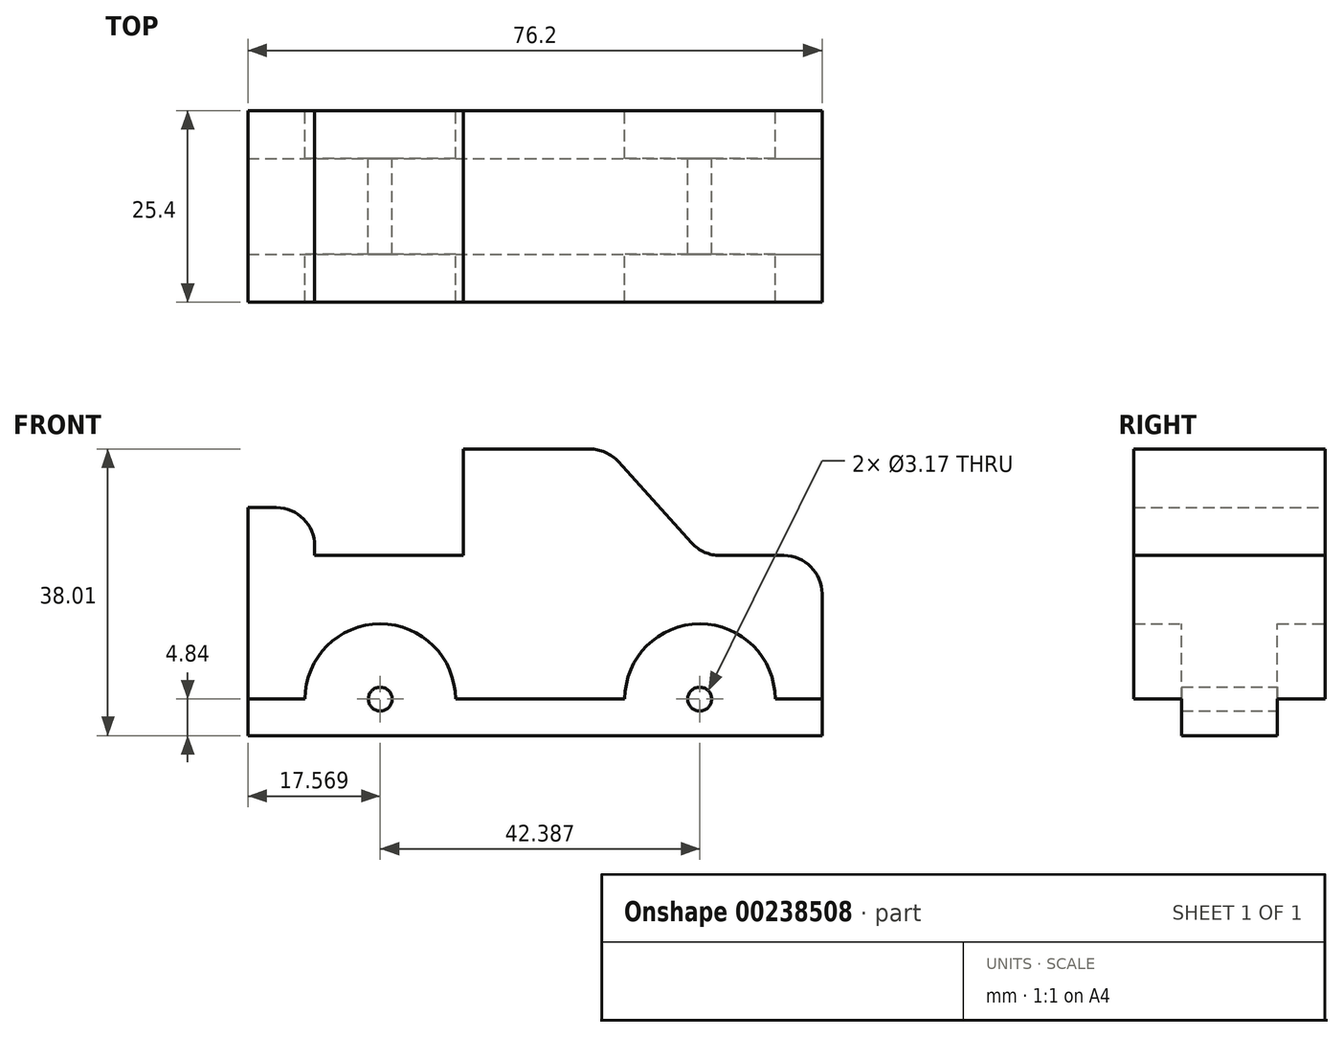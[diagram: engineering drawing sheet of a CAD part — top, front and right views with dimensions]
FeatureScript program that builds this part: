
annotation { "Feature Type Name" : "Feature", "Feature Type Description" : "" }
export const myFeature = defineFeature(function(context is Context, id is Id, definition is map)
    precondition{}
    {
        {
            var Q0;
            Q0=qCreatedBy(makeId("Front.planeOp"),FACE);
            var sketch = newSketch(context, id + "F0", { "sketchPlane" : qUnion([Q0])});
            skLineSegment(sketch, "E0", {"start": v(-38.1, 25.4) * mm, "end": v(-38.1, 0) * mm});
            skLineSegment(sketch, "E1", {"start": v(-38.1, 0) * mm, "end": v(38.1, 0) * mm});
            skLineSegment(sketch, "E2", {"start": v(38.1, 0) * mm, "end": v(38.1, 19.05) * mm});
            skLineSegment(sketch, "E3", {"start": v(38.1, 19.05) * mm, "end": v(22.33, 19.05) * mm});
            skLineSegment(sketch, "E4", {"start": v(22.33, 19.05) * mm, "end": v(9.54, 33.17) * mm});
            skLineSegment(sketch, "E5", {"start": v(9.54, 33.17) * mm, "end": v(-9.51, 33.17) * mm});
            skLineSegment(sketch, "E6", {"start": v(-9.51, 33.17) * mm, "end": v(-9.51, 19.05) * mm});
            skLineSegment(sketch, "E7", {"start": v(-9.51, 19.05) * mm, "end": v(-29.23, 19.05) * mm});
            skLineSegment(sketch, "E8", {"start": v(-29.23, 19.05) * mm, "end": v(-29.23, 25.4) * mm});
            skLineSegment(sketch, "E9", {"start": v(-29.23, 25.4) * mm, "end": v(-38.1, 25.4) * mm});
            skArc(sketch, "E10", {"start": v(-10.55, 0) * mm, "mid": v(-20.53, 9.98) * mm, "end": v(-30.5, 0) * mm});
            skArc(sketch, "E11", {"start": v(31.87, 0) * mm, "mid": v(21.9, 9.98) * mm, "end": v(11.92, 0) * mm});
            skPoint(sketch, "E12", {"position": v(0, 0) * mm});
            skSolve(sketch);
        }
        {
            var Q0;
            {var subQ0=sQuery(id+"F0.wireOp",EDGE,"E0");Q0=makeQuery(id+"F0.imprint","IMPRINT",FACE,{"disambiguationData":[TD([[makeQuery(id+"F0.imprint","IMPRINT",EDGE,{"derivedFrom":subQ0}),1.0]])]});}
            extrude(context, id + "F1", {"entities" : qUnion([Q0]), "depth" : 6.35 * mm});
        }
        {
            var Q0;
            Q0=makeQuery(id+"F1.opExtrude","CAP_FACE",FACE,{"disambiguationData":[OSD([sQuery(id+"F0.wireOp",EDGE,"E0"),sQuery(id+"F0.wireOp",EDGE,"E1"),sQuery(id+"F0.wireOp",EDGE,"E2"),sQuery(id+"F0.wireOp",EDGE,"E3"),sQuery(id+"F0.wireOp",EDGE,"E4"),sQuery(id+"F0.wireOp",EDGE,"E5"),sQuery(id+"F0.wireOp",EDGE,"E6"),sQuery(id+"F0.wireOp",EDGE,"E7"),sQuery(id+"F0.wireOp",EDGE,"E8"),sQuery(id+"F0.wireOp",EDGE,"E9"),sQuery(id+"F0.wireOp",EDGE,"E10"),sQuery(id+"F0.wireOp",EDGE,"E11")])],"isStart":false});
            var sketch = newSketch(context, id + "F2", { "sketchPlane" : qUnion([Q0])});
            skLineSegment(sketch, "E13", {"start": v(-38.1, 25.4) * mm, "end": v(-29.23, 25.4) * mm});
            skLineSegment(sketch, "E14", {"start": v(-29.23, 25.4) * mm, "end": v(-29.23, 19.05) * mm});
            skLineSegment(sketch, "E15", {"start": v(-29.23, 19.05) * mm, "end": v(-9.51, 19.05) * mm});
            skLineSegment(sketch, "E16", {"start": v(-9.51, 19.05) * mm, "end": v(-9.51, 33.17) * mm});
            skLineSegment(sketch, "E17", {"start": v(-9.51, 33.17) * mm, "end": v(9.54, 33.17) * mm});
            skLineSegment(sketch, "E18", {"start": v(9.54, 33.17) * mm, "end": v(22.33, 19.05) * mm});
            skLineSegment(sketch, "E19", {"start": v(22.33, 19.05) * mm, "end": v(38.1, 19.05) * mm});
            skLineSegment(sketch, "E20", {"start": v(38.1, 0) * mm, "end": v(-38.1, 0) * mm});
            skCircle(sketch, "E21", {"center": v(-20.53, 0) * mm, "radius": 1.59 * mm});
            skPoint(sketch, "E21.centerSnap0", {"position": v(-20.53, 9.98) * mm});
            skCircle(sketch, "E22", {"center": v(21.86, 0) * mm, "radius": 1.59 * mm});
            skLineSegment(sketch, "E23", {"start": v(-38.1, 25.4) * mm, "end": v(-38.1, -4.84) * mm});
            skLineSegment(sketch, "E24", {"start": v(-38.1, -4.84) * mm, "end": v(38.1, -4.84) * mm});
            skLineSegment(sketch, "E25", {"start": v(38.1, -4.84) * mm, "end": v(38.1, 19.05) * mm});
            skLineSegment(sketch, "E26", {"start": v(-38.1, 0) * mm, "end": v(38.1, 0) * mm, "construction": true});
            skSolve(sketch);
        }
        {
            var Q0;
            Q0 = qSketchRegion(id + "F2", true);
            extrude(context, id + "F3", {"entities" : qUnion([Q0]), "operationType" : NewBodyOperationType.ADD, "depth" : 12.7 * mm});
        }
        {
            var Q0;
            Q0=makeQuery(id+"F3.opExtrude","CAP_FACE",FACE,{"disambiguationData":[OSD([sQuery(id+"F2.wireOp",EDGE,"E13"),sQuery(id+"F2.wireOp",EDGE,"E14"),sQuery(id+"F2.wireOp",EDGE,"E15"),sQuery(id+"F2.wireOp",EDGE,"E16"),sQuery(id+"F2.wireOp",EDGE,"E17"),sQuery(id+"F2.wireOp",EDGE,"E18"),sQuery(id+"F2.wireOp",EDGE,"E19"),sQuery(id+"F2.wireOp",EDGE,"w17lI1Gz-qhxq-cBjz-HP93-S3bPv5mlDmBb"),sQuery(id+"F2.wireOp",EDGE,"E20"),sQuery(id+"F2.wireOp",EDGE,"CEwaxwHc-tyHI-bZ0t-qN4q-gG1szVgwZ8eV")])],"isStart":false});
            var sketch = newSketch(context, id + "F4", { "sketchPlane" : qUnion([Q0])});
            skLineSegment(sketch, "E27", {"start": v(-38.1, 25.4) * mm, "end": v(-38.1, 0) * mm});
            skLineSegment(sketch, "E28", {"start": v(38.1, 0) * mm, "end": v(38.1, 19.05) * mm});
            skLineSegment(sketch, "E29", {"start": v(38.1, 19.05) * mm, "end": v(22.33, 19.05) * mm});
            skLineSegment(sketch, "E30", {"start": v(22.33, 19.05) * mm, "end": v(9.54, 33.17) * mm});
            skLineSegment(sketch, "E31", {"start": v(9.54, 33.17) * mm, "end": v(-9.51, 33.17) * mm});
            skLineSegment(sketch, "E32", {"start": v(-9.51, 33.17) * mm, "end": v(-9.51, 19.05) * mm});
            skLineSegment(sketch, "E33", {"start": v(-9.51, 19.05) * mm, "end": v(-29.23, 19.05) * mm});
            skLineSegment(sketch, "E34", {"start": v(-29.23, 19.05) * mm, "end": v(-29.23, 25.4) * mm});
            skLineSegment(sketch, "E35", {"start": v(-29.23, 25.4) * mm, "end": v(-38.1, 25.4) * mm});
            skArc(sketch, "E36", {"start": v(-10.55, 0) * mm, "mid": v(-20.53, 9.98) * mm, "end": v(-30.5, 0) * mm});
            skArc(sketch, "E37", {"start": v(31.87, 0) * mm, "mid": v(21.9, 9.98) * mm, "end": v(11.92, 0) * mm});
            skPoint(sketch, "E38", {"position": v(-0.74, 0) * mm});
            skLineSegment(sketch, "E39", {"start": v(-38.1, 0) * mm, "end": v(38.1, 0) * mm});
            skPoint(sketch, "E40", {"position": v(0, 0) * mm});
            skSolve(sketch);
        }
        {
            var Q0;
            {var subQ1=sQuery(id+"F4.wireOp",EDGE,"E27");Q0=makeQuery(id+"F4.imprint","IMPRINT",FACE,{"disambiguationData":[TD([[makeQuery(id+"F4.imprint","IMPRINT",EDGE,{"derivedFrom":subQ1}),1.0]])]});}
            extrude(context, id + "F5", {"entities" : qUnion([Q0]), "operationType" : NewBodyOperationType.ADD, "depth" : 6.35 * mm});
        }
        {
            var Q0;
            Q0=makeQuery(id+"F5.boolean.opBoolean","MERGE",EDGE,{"derivedFrom":[makeQuery(id+"F3.boolean.opBoolean","MERGE",EDGE,{"derivedFrom":[makeQuery(id+"F1.opExtrude","SWEPT_EDGE",EDGE,{"disambiguationData":[OSD([sQuery(id+"F0.wireOp",EDGE,"E8"),sQuery(id+"F0.wireOp",EDGE,"E9")])]}),makeQuery(id+"F3.opExtrude","SWEPT_EDGE",EDGE,{"disambiguationData":[OSD([sQuery(id+"F2.wireOp",EDGE,"E13"),sQuery(id+"F2.wireOp",EDGE,"E14")])]})]}),makeQuery(id+"F5.opExtrude","SWEPT_EDGE",EDGE,{"disambiguationData":[OSD([sQuery(id+"F4.wireOp",EDGE,"E34"),sQuery(id+"F4.wireOp",EDGE,"E35")])]})]});
            fillet(context, id + "F6", {"entities" : qUnion([Q0]), "radius" : 5.08 * mm, "tangentPropagation" : true, "allowEdgeOverflow" : false});
        }
        {
            var Q0;
            Q0=makeQuery(id+"F5.boolean.opBoolean","MERGE",EDGE,{"derivedFrom":[makeQuery(id+"F3.boolean.opBoolean","MERGE",EDGE,{"derivedFrom":[makeQuery(id+"F1.opExtrude","SWEPT_EDGE",EDGE,{"disambiguationData":[OSD([sQuery(id+"F0.wireOp",EDGE,"E4"),sQuery(id+"F0.wireOp",EDGE,"E5")])]}),makeQuery(id+"F3.opExtrude","SWEPT_EDGE",EDGE,{"disambiguationData":[OSD([sQuery(id+"F2.wireOp",EDGE,"E17"),sQuery(id+"F2.wireOp",EDGE,"E18")])]})]}),makeQuery(id+"F5.opExtrude","SWEPT_EDGE",EDGE,{"disambiguationData":[OSD([sQuery(id+"F4.wireOp",EDGE,"E30"),sQuery(id+"F4.wireOp",EDGE,"E31")])]})]});
            fillet(context, id + "F7", {"entities" : qUnion([Q0]), "radius" : 5.08 * mm, "tangentPropagation" : true, "allowEdgeOverflow" : false});
        }
        {
            var Q0;
            Q0=makeQuery(id+"F5.boolean.opBoolean","MERGE",EDGE,{"derivedFrom":[makeQuery(id+"F3.boolean.opBoolean","MERGE",EDGE,{"derivedFrom":[makeQuery(id+"F1.opExtrude","SWEPT_EDGE",EDGE,{"disambiguationData":[OSD([sQuery(id+"F0.wireOp",EDGE,"E3"),sQuery(id+"F0.wireOp",EDGE,"E4")])]}),makeQuery(id+"F3.opExtrude","SWEPT_EDGE",EDGE,{"disambiguationData":[OSD([sQuery(id+"F2.wireOp",EDGE,"E18"),sQuery(id+"F2.wireOp",EDGE,"E19")])]})]}),makeQuery(id+"F5.opExtrude","SWEPT_EDGE",EDGE,{"disambiguationData":[OSD([sQuery(id+"F4.wireOp",EDGE,"E29"),sQuery(id+"F4.wireOp",EDGE,"E30")])]})]});
            var Q1;
            Q1=makeQuery(id+"F5.boolean.opBoolean","MERGE",EDGE,{"derivedFrom":[makeQuery(id+"F3.boolean.opBoolean","MERGE",EDGE,{"derivedFrom":[makeQuery(id+"F1.opExtrude","SWEPT_EDGE",EDGE,{"disambiguationData":[OSD([sQuery(id+"F0.wireOp",EDGE,"E2"),sQuery(id+"F0.wireOp",EDGE,"E3")])]}),makeQuery(id+"F3.opExtrude","SWEPT_EDGE",EDGE,{"disambiguationData":[OSD([sQuery(id+"F2.wireOp",EDGE,"E19"),sQuery(id+"F2.wireOp",EDGE,"E25")])]})]}),makeQuery(id+"F5.opExtrude","SWEPT_EDGE",EDGE,{"disambiguationData":[OSD([sQuery(id+"F4.wireOp",EDGE,"E28"),sQuery(id+"F4.wireOp",EDGE,"E29")])]})]});
            fillet(context, id + "F8", {"entities" : qUnion([Q0, Q1]), "radius" : 5.08 * mm, "tangentPropagation" : true, "allowEdgeOverflow" : false});
        }
    });
